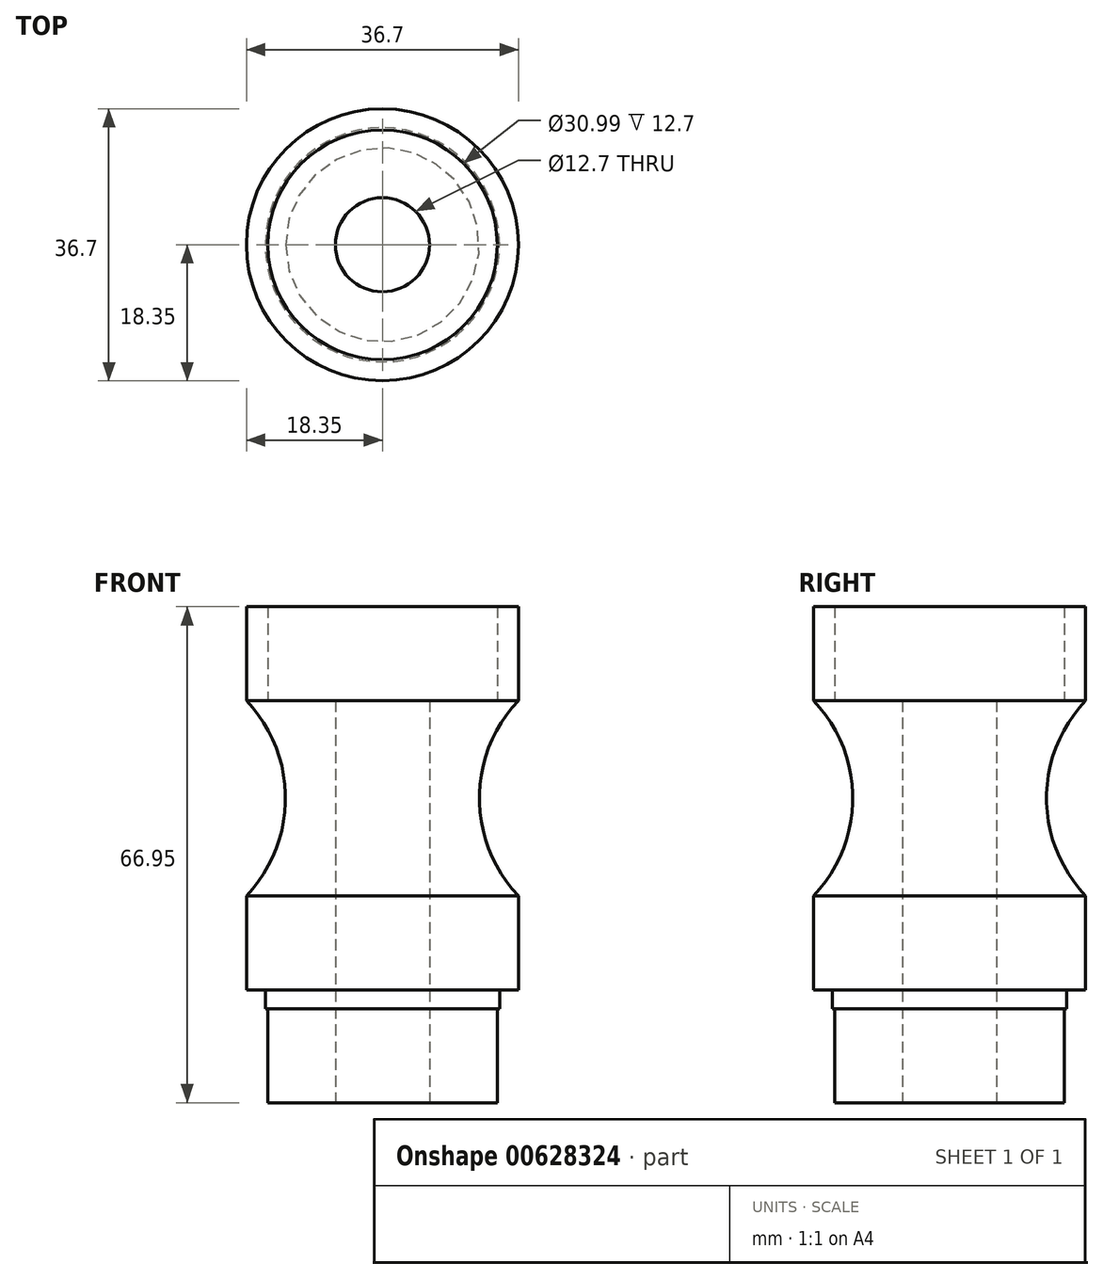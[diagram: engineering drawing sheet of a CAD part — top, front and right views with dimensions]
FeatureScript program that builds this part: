
annotation { "Feature Type Name" : "Feature", "Feature Type Description" : "" }
export const myFeature = defineFeature(function(context is Context, id is Id, definition is map)
    precondition{}
    {
        {
            var Q0;
            Q0=qCreatedBy(makeId("Front.planeOp"),FACE);
            var sketch = newSketch(context, id + "F0", { "sketchPlane" : qUnion([Q0])});
            skArc(sketch, "E0", {"start": v(18.35, 12.42) * mm, "mid": v(13.08, -0.73) * mm, "end": v(18.35, -13.89) * mm});
            skLineSegment(sketch, "E1", {"start": v(18.35, 12.42) * mm, "end": v(18.35, 25.12) * mm});
            skLineSegment(sketch, "E2", {"start": v(18.35, -13.89) * mm, "end": v(18.35, -26.59) * mm});
            skLineSegment(sketch, "E3", {"start": v(18.35, -26.59) * mm, "end": v(15.81, -26.59) * mm});
            skLineSegment(sketch, "E4", {"start": v(15.81, -26.59) * mm, "end": v(15.81, -29.13) * mm});
            skLineSegment(sketch, "E5", {"start": v(15.5, -29.13) * mm, "end": v(15.81, -29.13) * mm});
            skLineSegment(sketch, "E6", {"start": v(15.5, -29.13) * mm, "end": v(15.5, -41.83) * mm});
            skLineSegment(sketch, "E7", {"start": v(15.5, -41.83) * mm, "end": v(6.35, -41.83) * mm});
            skLineSegment(sketch, "E8", {"start": v(6.35, -41.83) * mm, "end": v(6.35, 12.42) * mm});
            skLineSegment(sketch, "E9", {"start": v(15.5, 25.12) * mm, "end": v(18.35, 25.12) * mm});
            skLineSegment(sketch, "E10", {"start": v(15.5, 25.12) * mm, "end": v(15.5, 12.42) * mm});
            skLineSegment(sketch, "E11", {"start": v(15.5, 12.42) * mm, "end": v(6.35, 12.42) * mm});
            skLineSegment(sketch, "E12", {"start": v(0, -34.35) * mm, "end": v(0, 14.35) * mm});
            skSolve(sketch);
        }
        {
            var Q0;
            Q0=makeQuery(id+"F0.imprint","IMPRINT",FACE,{"disambiguationData":[TD([[makeQuery(id+"F0.imprint","IMPRINT",EDGE,{"derivedFrom":sQuery(id+"F0.wireOp",EDGE,"E0")}),-1.0]])]});
            var Q1;
            Q1=sQuery(id+"F0.wireOp",EDGE,"E12");
            revolve(context, id + "F1", {"entities" : qUnion([Q0]), "axis" : qUnion([Q1]), "revolveType" : RevolveType.FULL});
        }
    });
